# Revit family: RFA_LBL-MA2000_B1
name_source: partatom
category: Plumbing Fixtures
revit_build: Autodesk Revit Architecture 2012 (Build: 20110309_2315(x64)
units: mm (PartAtom-declared; Revit-internal decimal feet)

## types (1)
- LBL_MA7000_Vitreous China White
    Assembly Code = D2010110
    CW Connection = Yes
    CWFU = 0
    Cold Water Connector = Cold Water Connection
    Cold Water Diameter = 0"
    Cold Water Radius = 0"
    Default Elevation = 0' - 0"
    Description = Little Bottom Line 'The Start-Up'
    Finish = LBL_Vitreous China
    Flush Rate = 1.6 GPM
    Handle Material = LBL_Stainless - Polished
    Height = 1' - 9 27/32"
    Length = 1' - 8 21/32"
    Manufacturer = Little Bottom Line
    Model = MA2000
    Product Documentation Link = http://www.littlebottomlinellc.com
    Product Page URL = http://www.littlebottomlinellc.com
    Rough In = 1' - 0"
    Sanitary Connector = Sanitary Connection
    Sanitary Diameter = 2"
    Sanitary Radius = 1"
    URL = http://www.littlebottomlinellc.com
    WFU = 0
    Wall Offset = 0' - 1"
    Waste Connection = Yes
    Width = 0' - 11 7/32"

## geometry (parser evidence)
native form markers: Blend x12, Sweep x1
no freeform markers — native parametric forms only
